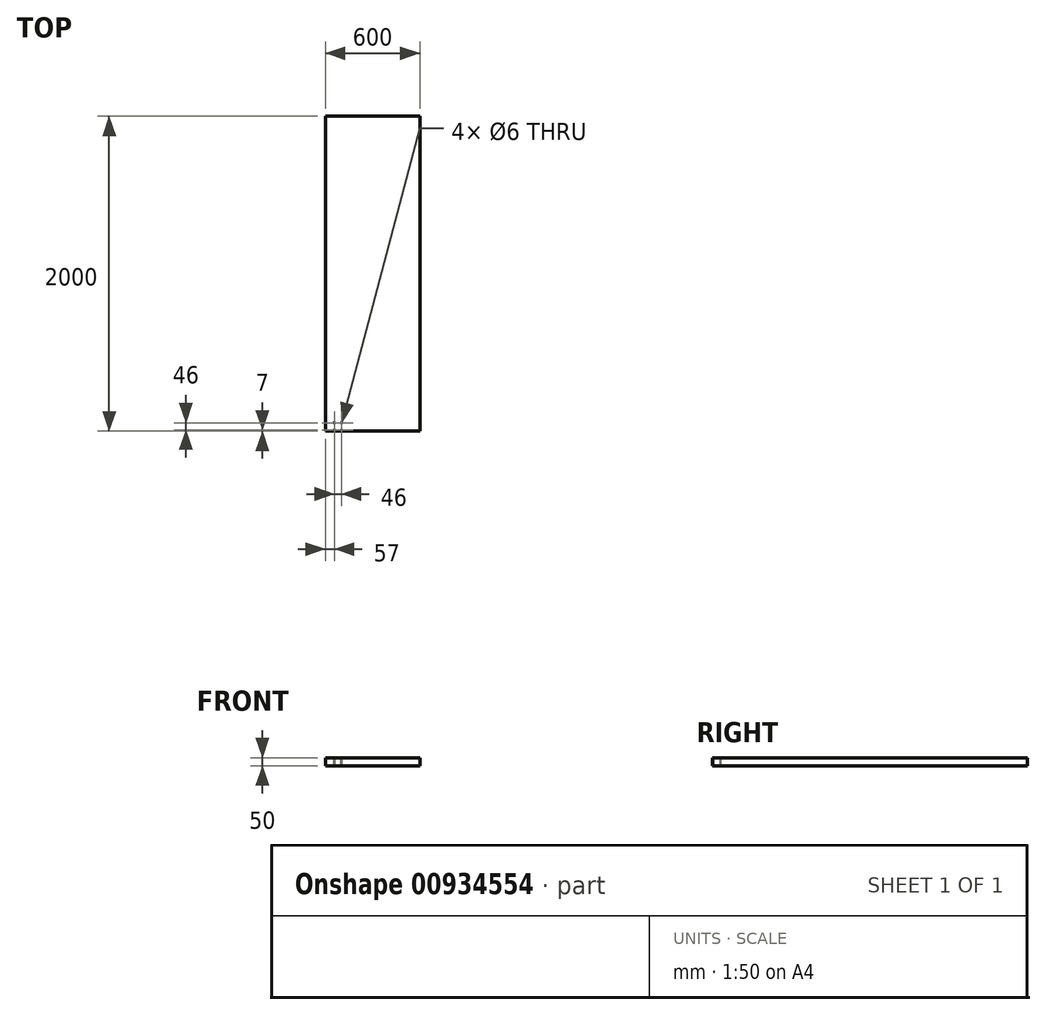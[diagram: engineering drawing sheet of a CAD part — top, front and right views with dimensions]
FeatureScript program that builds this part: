
annotation { "Feature Type Name" : "Feature", "Feature Type Description" : "" }
export const myFeature = defineFeature(function(context is Context, id is Id, definition is map)
    precondition{}
    {
        {
            var Q0;
            Q0=qCreatedBy(makeId("Top.planeOp"),FACE);
            var sketch = newSketch(context, id + "F0", { "sketchPlane" : qUnion([Q0])});
            skLineSegment(sketch, "E0.bottom", {"start": v(300, 1000) * mm, "end": v(-300, 1000) * mm});
            skLineSegment(sketch, "E0.top", {"start": v(300, -1000) * mm, "end": v(-300, -1000) * mm});
            skLineSegment(sketch, "E0.left", {"start": v(300, 1000) * mm, "end": v(300, -1000) * mm});
            skLineSegment(sketch, "E0.right", {"start": v(-300, 1000) * mm, "end": v(-300, -1000) * mm});
            skPoint(sketch, "E0.middle", {"position": v(0, 0) * mm});
            skSolve(sketch);
        }
        {
            var Q0;
            Q0=makeQuery(id+"F0.imprint","IMPRINT",FACE,{"disambiguationData":[TD([[makeQuery(id+"F0.imprint","IMPRINT",EDGE,{"derivedFrom":sQuery(id+"F0.wireOp",EDGE,"E0.bottom")}),1.0]])]});
            extrude(context, id + "F1", {"entities" : qUnion([Q0]), "depth" : 50 * mm, "offsetDistance" : 25 * mm});
        }
        {
            var Q0;
            Q0=makeQuery(id+"F1.opExtrude","CAP_FACE",FACE,{"disambiguationData":[OSD([sQuery(id+"F0.wireOp",EDGE,"E0.bottom"),sQuery(id+"F0.wireOp",EDGE,"E0.top"),sQuery(id+"F0.wireOp",EDGE,"E0.left"),sQuery(id+"F0.wireOp",EDGE,"E0.right")])],"isStart":false});
            var sketch = newSketch(context, id + "F2", { "sketchPlane" : qUnion([Q0])});
            skLineSegment(sketch, "E1.bottom", {"start": v(-250, -1000) * mm, "end": v(-190, -1000) * mm, "construction": true});
            skLineSegment(sketch, "E1.top", {"start": v(-250, -940) * mm, "end": v(-190, -940) * mm, "construction": true});
            skLineSegment(sketch, "E1.left", {"start": v(-250, -1000) * mm, "end": v(-250, -940) * mm, "construction": true});
            skLineSegment(sketch, "E1.right", {"start": v(-190, -1000) * mm, "end": v(-190, -940) * mm, "construction": true});
            skLineSegment(sketch, "E2.0", {"start": v(-243, -993) * mm, "end": v(-243, -947) * mm, "construction": true});
            skLineSegment(sketch, "E2.1", {"start": v(-243, -993) * mm, "end": v(-197, -993) * mm, "construction": true});
            skLineSegment(sketch, "E2.2", {"start": v(-197, -993) * mm, "end": v(-197, -947) * mm, "construction": true});
            skLineSegment(sketch, "E2.3", {"start": v(-243, -947) * mm, "end": v(-197, -947) * mm, "construction": true});
            skCircle(sketch, "E3", {"center": v(-243, -947) * mm, "radius": 3 * mm});
            skCircle(sketch, "E4.0.1.0", {"center": v(-243, -993) * mm, "radius": 3 * mm});
            skCircle(sketch, "E4.1.0.0", {"center": v(-197, -947) * mm, "radius": 3 * mm});
            skCircle(sketch, "E4.1.1.0", {"center": v(-197, -993) * mm, "radius": 3 * mm});
            skLineSegment(sketch, "E4.direction2", {"start": v(-243, -947) * mm, "end": v(-243, -993) * mm, "construction": true});
            skSolve(sketch);
        }
        {
            var Q0;
            Q0 = qSketchRegion(id + "F2", true);
            extrude(context, id + "F3", {"entities" : qUnion([Q0]), "operationType" : NewBodyOperationType.REMOVE, "endBound" : BoundingType.THROUGH_ALL, "oppositeDirection" : true, "depth" : 25 * mm, "offsetDistance" : 25 * mm});
        }
    });
